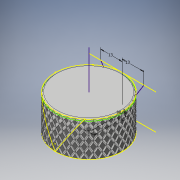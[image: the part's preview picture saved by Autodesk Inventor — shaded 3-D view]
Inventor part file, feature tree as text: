
AUTODESK INVENTOR PART (.ipt)
format: ipt  version: 2018 (Build 220112000, 112)  size: 3,618,816 bytes
history: native  units: mm
features: sketch x8, other x5, extrude x4, sweep x2, reference x2, plane x1, chamfer x1, fillet x1, pattern_circular x1, projected_geometry x1
ambient origin geometry x8: Origin, YZ Plane, XZ Plane, XY Plane, X Axis, Y Axis, Z Axis, Center Point
bodies: Volumenkörper1 (feature_tree)
feature tree (26):
  extrude  "Extrusion1"  Depth=16.0mm TaperAngle=0.0deg
  sketch  "Skizze2"  dims[d3=1.0mm d4=0.0mm d5=1.0mm]
  extrude  "Extrusion2"  Depth=1.0mm
  extrude  "Extrusion3"  Depth=7.0mm TaperAngle=45.0deg
  plane  "Arbeitsebene1"
  extrude  "Extrusion5"  Depth=10.0mm
  chamfer  "Fase4"  Distance=10.0mm
  fillet  "Rundung2"  Radius=13.0mm
  sketch  "Skizze9"  dims[d44=90.0deg d45=0.0mm]
  sketch  "Skizze10"  dims[d46=3.0mm]
  other  "3D-Skizze2"
  sweep  "Sweeping4"
  pattern_circular  "Runde Anordnung2"  [2 undecoded]
  sketch  "Skizze11"  dims[d47=19.5mm]
  sketch  "Skizze13"  dims[d50=13.0mm d51=0.0mm d52=0.0mm d53=320.0mm d54=360.0deg d56=1.0mm d57=1.0mm d58=0.0mm d59=0.0mm]
  sweep  "Sweeping5"
  sketch  "Skizze1"  dims[d0=0.05mm d1=16.0mm d2=0.0mm]
  reference  "Referenz1"
  reference  "Referenz2"
  sketch  "Skizze3"  dims[d6=20.0mm d7=0.0mm d25=7.0mm d26=16.0mm d27=45.0deg]
  sketch  "Skizze5"  dims[d28=17.25mm d30=1.0mm d31=10.0mm d32=0.0mm d43=13.0mm]
  projected_geometry  "Projizierte Kontur1"
  other  "Projekt aus Skizze9"
  other  "3D-Skizze3"
  parser-record x1  (decoder bookkeeping rows leaked as tree rows — omitted from the tree; the rows remain in map.json)
  other  "VolumeKnob.iam"
note: 2 required parameter values undecoded (feature->parameter linkage not recoverable at this tier; creation-order binding heuristic only, values carry confidence <= 0.55)
note: 1 file-system path scrubbed to <path> (originals preserved in map.json)
